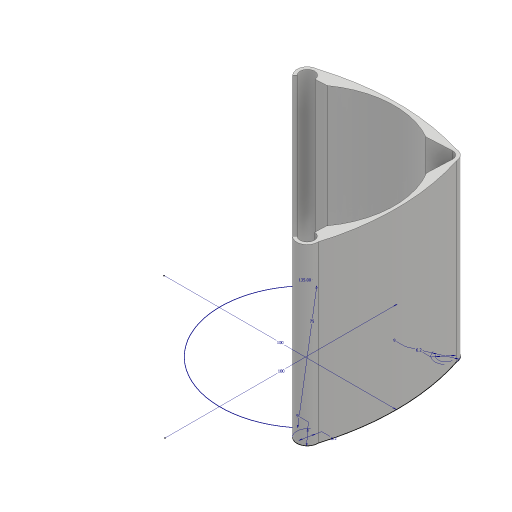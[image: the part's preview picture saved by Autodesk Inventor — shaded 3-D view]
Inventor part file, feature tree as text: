
AUTODESK INVENTOR PART (.ipt)
format: ipt  version: 2023 (Build 270158000, 158)  size: 133,120 bytes
history: native  units: mm
features: extrude x1, sketch x1
ambient origin geometry x8: Origin, YZ Plane, XZ Plane, XY Plane, X Axis, Y Axis, Z Axis, Center Point
bodies: Solid1 (feature_tree)
feature tree (2):
  extrude  "Extrusion1"  Depth=75.0mm
  sketch  "Sketch1"  dims[d0=6.2mm d1=6.2mm d6=9.0mm d7=9.0mm d8=135.0deg d9=75.0mm d11=100.0mm d12=100.0mm d13=75.0mm d14=0.0mm]
